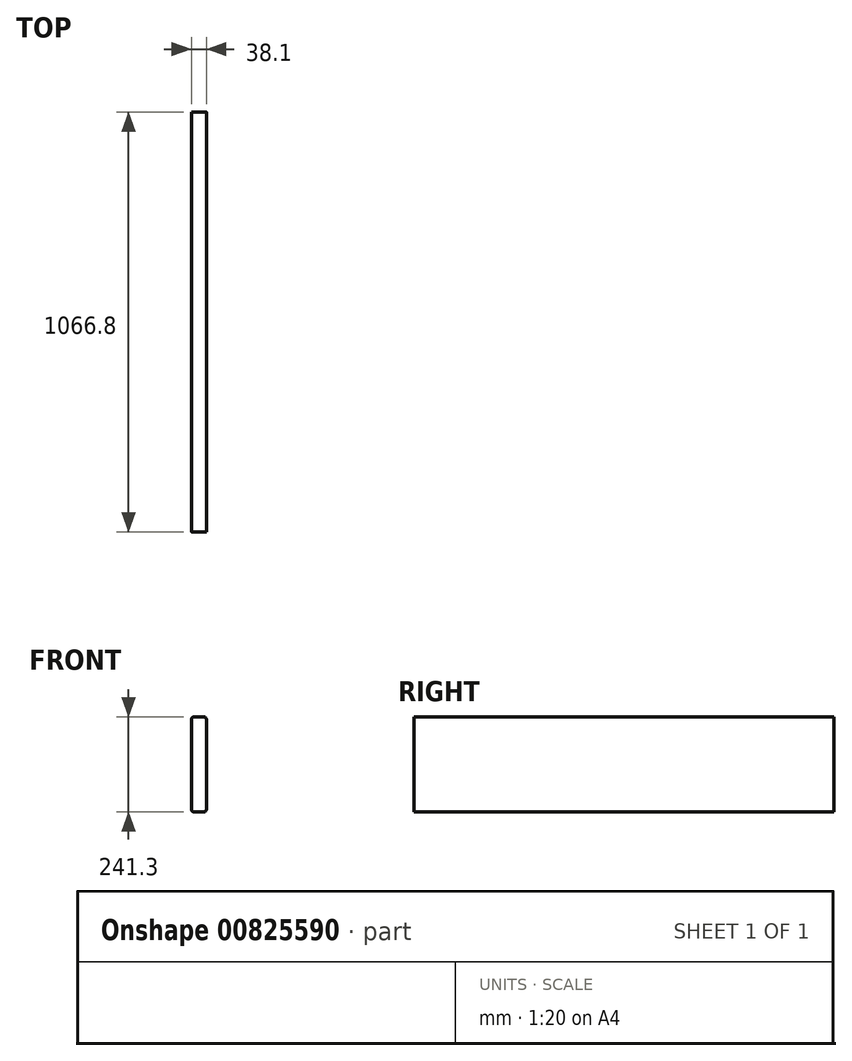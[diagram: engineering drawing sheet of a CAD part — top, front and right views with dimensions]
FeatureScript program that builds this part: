
annotation { "Feature Type Name" : "Feature", "Feature Type Description" : "" }
export const myFeature = defineFeature(function(context is Context, id is Id, definition is map)
    precondition{}
    {
        {
            var Q0;
            Q0=qCreatedBy(makeId("Front.planeOp"),FACE);
            var sketch = newSketch(context, id + "F0", { "sketchPlane" : qUnion([Q0])});
            skLineSegment(sketch, "E0.bottom", {"start": v(12.7, 120.65) * mm, "end": v(-12.7, 120.65) * mm});
            skLineSegment(sketch, "E0.top", {"start": v(12.7, -120.65) * mm, "end": v(-12.7, -120.65) * mm});
            skLineSegment(sketch, "E0.left", {"start": v(19.05, 114.3) * mm, "end": v(19.05, -114.3) * mm});
            skLineSegment(sketch, "E0.right", {"start": v(-19.05, 114.3) * mm, "end": v(-19.05, -114.3) * mm});
            skPoint(sketch, "E0.middle", {"position": v(0, 0) * mm});
            skPoint(sketch, "E1.visualSharp", {"position": v(-19.05, 120.65) * mm});
            skArc(sketch, "E1.filletArc", {"start": v(-12.7, 120.65) * mm, "mid": v(-17.2, 118.8) * mm, "end": v(-19.05, 114.3) * mm});
            skPoint(sketch, "E2.visualSharp", {"position": v(19.05, 120.65) * mm});
            skArc(sketch, "E2.filletArc", {"start": v(19.05, 114.3) * mm, "mid": v(17.2, 118.8) * mm, "end": v(12.7, 120.65) * mm});
            skPoint(sketch, "E3.visualSharp", {"position": v(19.05, -120.65) * mm});
            skArc(sketch, "E3.filletArc", {"start": v(12.7, -120.65) * mm, "mid": v(17.2, -118.8) * mm, "end": v(19.05, -114.3) * mm});
            skPoint(sketch, "E4.visualSharp", {"position": v(-19.05, -120.65) * mm});
            skArc(sketch, "E4.filletArc", {"start": v(-19.05, -114.3) * mm, "mid": v(-17.2, -118.8) * mm, "end": v(-12.7, -120.65) * mm});
            skSolve(sketch);
        }
        {
            var Q0;
            Q0=makeQuery(id+"F0.imprint","IMPRINT",FACE,{"disambiguationData":[TD([[makeQuery(id+"F0.imprint","IMPRINT",EDGE,{"derivedFrom":sQuery(id+"F0.wireOp",EDGE,"E0.bottom")}),1.0]])]});
            extrude(context, id + "F1", {"entities" : qUnion([Q0]), "endBound" : BoundingType.SYMMETRIC, "depth" : 1066.8 * mm, "offsetDistance" : 25.4 * mm});
        }
    });
